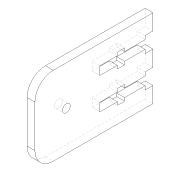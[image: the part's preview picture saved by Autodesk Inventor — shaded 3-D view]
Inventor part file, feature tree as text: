
AUTODESK INVENTOR PART (.ipt)
format: ipt  version: 2016 (Build 200138000, 138)  size: 159,232 bytes
history: native  units: mm
features: extrude x3, sketch x3, fillet x1
ambient origin geometry x8: Origin, YZ Plane, XZ Plane, XY Plane, X Axis, Y Axis, Z Axis, Center Point
bodies: Solid1 (feature_tree)
feature tree (7):
  extrude  "Extrusion1"  Depth=30.0mm
  extrude  "Extrusion2"  Depth=6.0mm
  fillet  "Fillet1"  Radius=6.0mm
  extrude  "Extrusion3"  Depth=7.0mm
  sketch  "Sketch1"  dims[d0=45.0mm d1=30.0mm]
  sketch  "Sketch2"  dims[d2=3.0mm d3=0.0mm d4=6.0mm d6=6.0mm]
  sketch  "Sketch3"  dims[d7=4.0mm d8=0.0mm d9=7.0mm d10=3.0mm d11=15.0mm d12=12.0mm d13=4.0mm d14=0.0mm d18=6.0mm d19=3.0mm d20=6.0mm d21=6.0mm d22=1.4mm d23=7.8mm d24=1.2mm d25=2.75mm d26=1.2mm d27=6.65mm d28=3.2mm d29=1.2mm d30=1.4mm d31=1.2mm d32=3.2mm d33=1.2mm d34=20.2mm]
